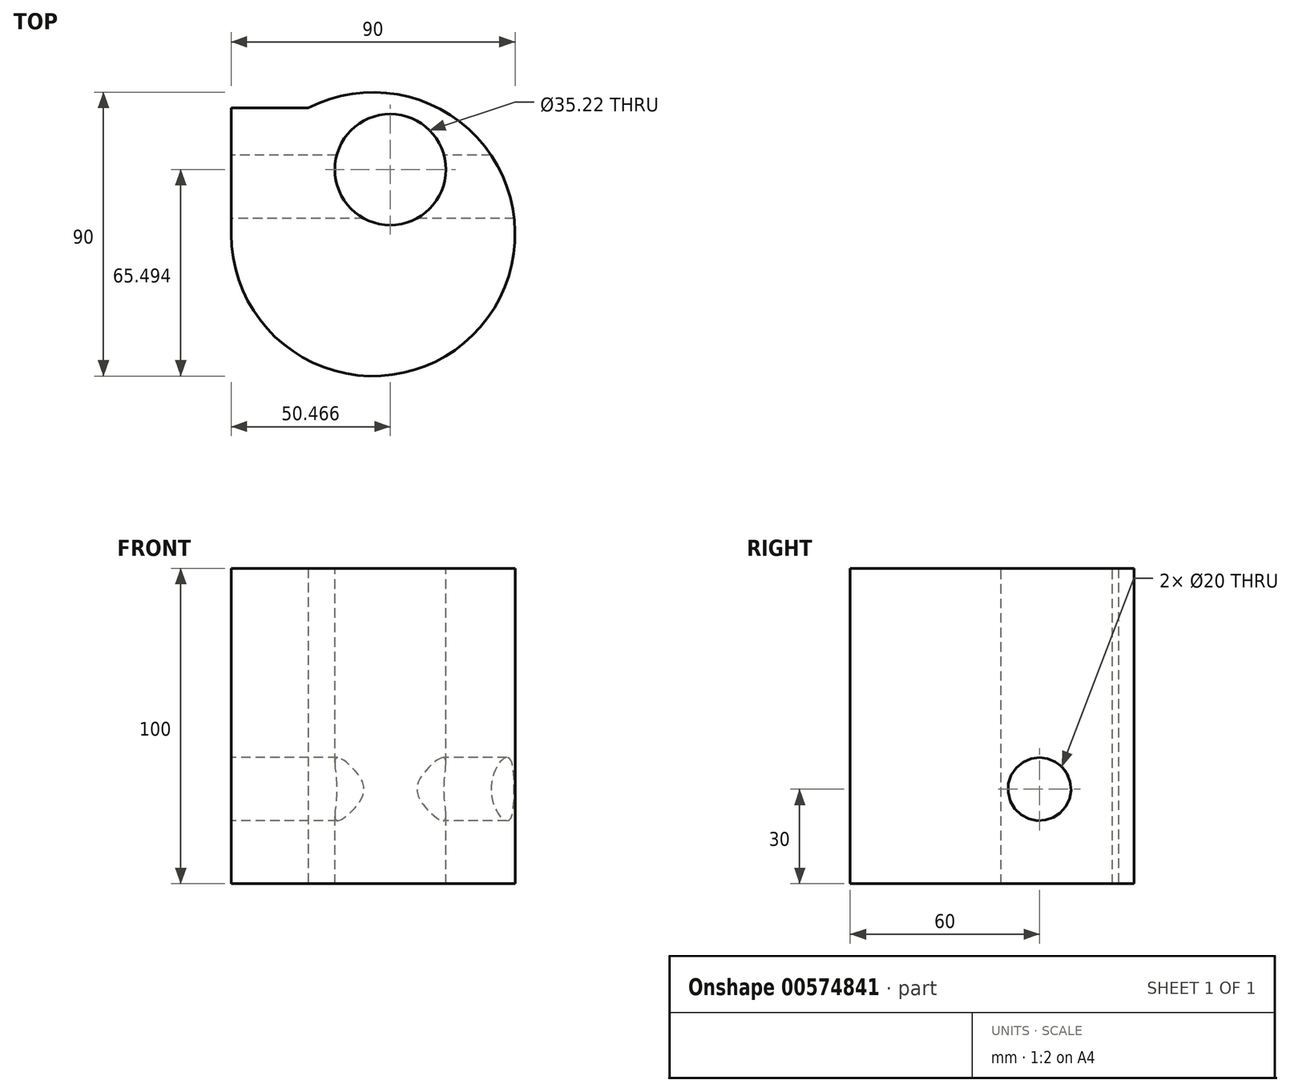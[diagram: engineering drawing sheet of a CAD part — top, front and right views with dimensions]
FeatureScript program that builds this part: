
annotation { "Feature Type Name" : "Feature", "Feature Type Description" : "" }
export const myFeature = defineFeature(function(context is Context, id is Id, definition is map)
    precondition{}
    {
        {
            var Q0;
            Q0=qCreatedBy(makeId("Top.planeOp"),FACE);
            var sketch = newSketch(context, id + "F0", { "sketchPlane" : qUnion([Q0])});
            skCircle(sketch, "E0", {"center": v(0, 0) * mm, "radius": 45 * mm});
            skLineSegment(sketch, "E1.bottom", {"start": v(-45, 40) * mm, "end": v(0, 40) * mm});
            skLineSegment(sketch, "E1.top", {"start": v(-45, 0) * mm, "end": v(0, 0) * mm});
            skLineSegment(sketch, "E1.left", {"start": v(-45, 40) * mm, "end": v(-45, 0) * mm});
            skLineSegment(sketch, "E1.right", {"start": v(0, 40) * mm, "end": v(0, 0) * mm});
            skSolve(sketch);
        }
        {
            var Q0;
            Q0 = qSketchRegion(id + "F0", true);
            extrude(context, id + "F1", {"entities" : qUnion([Q0]), "depth" : 100 * mm, "offsetDistance" : 25 * mm});
        }
        {
            var Q0;
            Q0=makeQuery(id+"F1.opExtrude","CAP_FACE",FACE,{"disambiguationData":[OSD([sQuery(id+"F0.wireOp",EDGE,"E0"),sQuery(id+"F0.wireOp",EDGE,"E1.bottom"),sQuery(id+"F0.wireOp",EDGE,"E1.left")])],"isStart":false});
            var sketch = newSketch(context, id + "F2", { "sketchPlane" : qUnion([Q0])});
            skCircle(sketch, "E2", {"center": v(5.47, 20.5) * mm, "radius": 17.61 * mm});
            skSolve(sketch);
        }
        {
            var Q0;
            Q0 = qSketchRegion(id + "F2", true);
            extrude(context, id + "F3", {"entities" : qUnion([Q0]), "operationType" : NewBodyOperationType.REMOVE, "endBound" : BoundingType.THROUGH_ALL, "oppositeDirection" : true, "depth" : 25 * mm, "offsetDistance" : 25 * mm});
        }
        {
            var Q0;
            Q0=makeQuery(id+"F1.opExtrude","SWEPT_FACE",FACE,{"disambiguationData":[OSD([sQuery(id+"F0.wireOp",EDGE,"E1.left")])]});
            var sketch = newSketch(context, id + "F4", { "sketchPlane" : qUnion([Q0])});
            skCircle(sketch, "E3", {"center": v(-15, 30) * mm, "radius": 10 * mm});
            skSolve(sketch);
        }
        {
            var Q0;
            Q0 = qSketchRegion(id + "F4", true);
            extrude(context, id + "F5", {"entities" : qUnion([Q0]), "operationType" : NewBodyOperationType.REMOVE, "endBound" : BoundingType.THROUGH_ALL, "oppositeDirection" : true, "depth" : 25 * mm, "offsetDistance" : 25 * mm});
        }
    });
